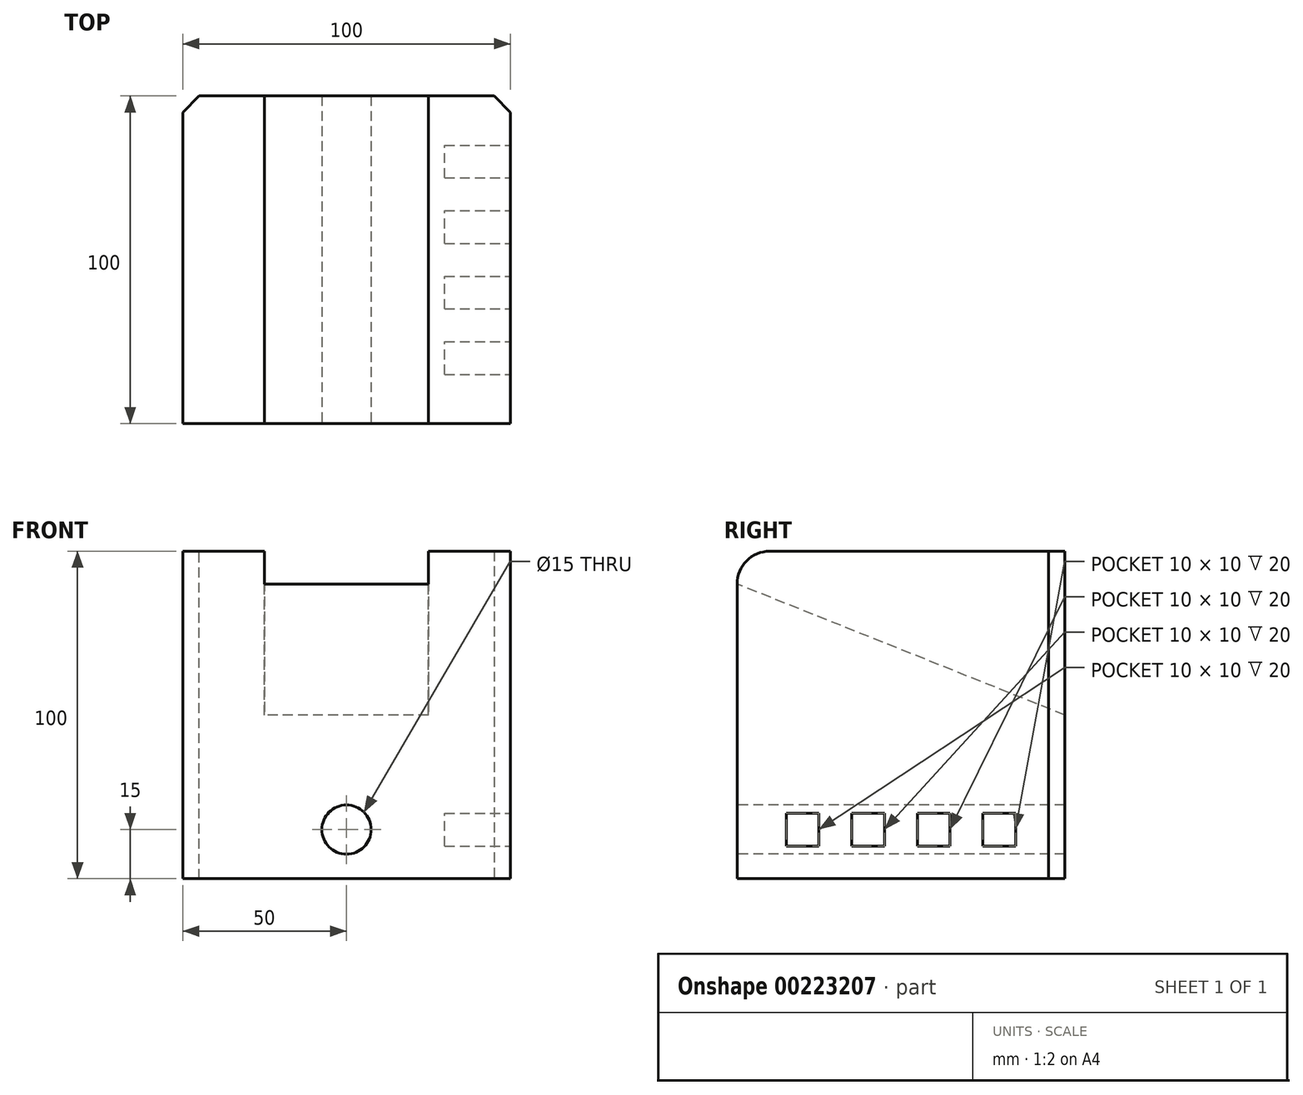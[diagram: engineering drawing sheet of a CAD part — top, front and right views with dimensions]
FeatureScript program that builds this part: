
annotation { "Feature Type Name" : "Feature", "Feature Type Description" : "" }
export const myFeature = defineFeature(function(context is Context, id is Id, definition is map)
    precondition{}
    {
        {
            var Q0;
            Q0=qCreatedBy(makeId("Front.planeOp"),FACE);
            var sketch = newSketch(context, id + "F0", { "sketchPlane" : qUnion([Q0])});
            skLineSegment(sketch, "E0.bottom", {"start": v(0, 0) * mm, "end": v(-100, 0) * mm});
            skLineSegment(sketch, "E0.top", {"start": v(0, 100) * mm, "end": v(-100, 100) * mm});
            skLineSegment(sketch, "E0.left", {"start": v(0, 0) * mm, "end": v(0, 100) * mm});
            skLineSegment(sketch, "E0.right", {"start": v(-100, 0) * mm, "end": v(-100, 100) * mm});
            skLineSegment(sketch, "E1", {"start": v(0, 0) * mm, "end": v(-50, 0) * mm, "construction": true});
            skLineSegment(sketch, "E2", {"start": v(-50, 0) * mm, "end": v(-50, 15) * mm, "construction": true});
            skCircle(sketch, "E3", {"center": v(-50, 15) * mm, "radius": 7.5 * mm});
            skSolve(sketch);
        }
        {
            var Q0;
            Q0 = qSketchRegion(id + "F0", true);
            extrude(context, id + "F1", {"entities" : qUnion([Q0]), "oppositeDirection" : true, "depth" : 100 * mm});
        }
        {
            var Q0;
            Q0=makeQuery(id+"F1.opExtrude","SWEPT_FACE",FACE,{"disambiguationData":[OSD([sQuery(id+"F0.wireOp",EDGE,"E0.left")])]});
            var Q1;
            Q1=makeQuery(id+"F1.opExtrude","SWEPT_FACE",FACE,{"disambiguationData":[OSD([sQuery(id+"F0.wireOp",EDGE,"E0.right")])]});
            cPlane(context, id + "F2", {"entities" : qUnion([Q0, Q1]), "cplaneType" : CPlaneType.MID_PLANE, "offset" : 25 * mm, "width" : 150 * mm, "height" : 150 * mm});
        }
        {
            var Q0;
            Q0=qCreatedBy(id+"F2.planeOp",FACE);
            var sketch = newSketch(context, id + "F3", { "sketchPlane" : qUnion([Q0])});
            skLineSegment(sketch, "E4", {"start": v(0, 90) * mm, "end": v(0, 100) * mm});
            skLineSegment(sketch, "E5", {"start": v(0, 100) * mm, "end": v(100, 100) * mm});
            skLineSegment(sketch, "E6", {"start": v(100, 100) * mm, "end": v(100, 50) * mm});
            skLineSegment(sketch, "E7", {"start": v(100, 50) * mm, "end": v(0, 90) * mm});
            skLineSegment(sketch, "E8", {"start": v(0, 90) * mm, "end": v(0, 0) * mm, "construction": true});
            skSolve(sketch);
        }
        {
            var Q0;
            Q0 = qSketchRegion(id + "F3", true);
            extrude(context, id + "F4", {"entities" : qUnion([Q0]), "operationType" : NewBodyOperationType.REMOVE, "endBound" : BoundingType.SYMMETRIC, "depth" : 50 * mm});
        }
        {
            var Q0;
            {var subQ0=sQuery(id+"F0.wireOp",EDGE,"E0.left");var subQ1=sQuery(id+"F0.wireOp",EDGE,"E0.top");Q0=makeQuery(id+"F4.boolean.opBoolean","SPLIT",EDGE,{"disambiguationData":[TD([makeQuery(id+"F1.opExtrude","SWEPT_FACE",FACE,{"disambiguationData":[OSD([subQ0])]})])],"derivedFrom":makeQuery(id+"F1.opExtrude","CAP_EDGE",EDGE,{"disambiguationData":[OSD([subQ1])],"isStart":true})});}
            var Q1;
            {var subQ0=sQuery(id+"F0.wireOp",EDGE,"E0.right");var subQ1=sQuery(id+"F0.wireOp",EDGE,"E0.top");Q1=makeQuery(id+"F4.boolean.opBoolean","SPLIT",EDGE,{"disambiguationData":[TD([makeQuery(id+"F1.opExtrude","SWEPT_FACE",FACE,{"disambiguationData":[OSD([subQ0])]})])],"derivedFrom":makeQuery(id+"F1.opExtrude","CAP_EDGE",EDGE,{"disambiguationData":[OSD([subQ1])],"isStart":true})});}
            fillet(context, id + "F5", {"entities" : qUnion([Q0, Q1]), "radius" : 10 * mm, "tangentPropagation" : true, "allowEdgeOverflow" : false});
        }
        {
            var Q0;
            Q0=makeQuery(id+"F1.opExtrude","CAP_EDGE",EDGE,{"disambiguationData":[OSD([sQuery(id+"F0.wireOp",EDGE,"E0.left")])],"isStart":false});
            var Q1;
            Q1=makeQuery(id+"F1.opExtrude","CAP_EDGE",EDGE,{"disambiguationData":[OSD([sQuery(id+"F0.wireOp",EDGE,"E0.right")])],"isStart":false});
            chamfer(context, id + "F6", {"entities" : qUnion([Q0, Q1]), "width" : 5 * mm, "tangentPropagation" : true});
        }
        {
            var Q0;
            Q0=qCreatedBy(makeId("Right.planeOp"),FACE);
            var sketch = newSketch(context, id + "F7", { "sketchPlane" : qUnion([Q0])});
            skLineSegment(sketch, "E9", {"start": v(0, 0) * mm, "end": v(15, 0) * mm, "construction": true});
            skLineSegment(sketch, "E10", {"start": v(15, 0) * mm, "end": v(15, 10) * mm, "construction": true});
            skLineSegment(sketch, "E11.bottom", {"start": v(15, 10) * mm, "end": v(25, 10) * mm});
            skLineSegment(sketch, "E11.top", {"start": v(15, 20) * mm, "end": v(25, 20) * mm});
            skLineSegment(sketch, "E11.left", {"start": v(15, 10) * mm, "end": v(15, 20) * mm});
            skLineSegment(sketch, "E11.right", {"start": v(25, 10) * mm, "end": v(25, 20) * mm});
            skLineSegment(sketch, "E12.1.0.0", {"start": v(35, 20) * mm, "end": v(45, 20) * mm});
            skLineSegment(sketch, "E12.1.0.1", {"start": v(45, 10) * mm, "end": v(45, 20) * mm});
            skLineSegment(sketch, "E12.1.0.2", {"start": v(35, 10) * mm, "end": v(45, 10) * mm});
            skLineSegment(sketch, "E12.1.0.3", {"start": v(35, 10) * mm, "end": v(35, 20) * mm});
            skLineSegment(sketch, "E12.2.0.0", {"start": v(55, 20) * mm, "end": v(65, 20) * mm});
            skLineSegment(sketch, "E12.2.0.1", {"start": v(65, 10) * mm, "end": v(65, 20) * mm});
            skLineSegment(sketch, "E12.2.0.2", {"start": v(55, 10) * mm, "end": v(65, 10) * mm});
            skLineSegment(sketch, "E12.2.0.3", {"start": v(55, 10) * mm, "end": v(55, 20) * mm});
            skLineSegment(sketch, "E12.3.0.0", {"start": v(75, 20) * mm, "end": v(85, 20) * mm});
            skLineSegment(sketch, "E12.3.0.1", {"start": v(85, 10) * mm, "end": v(85, 20) * mm});
            skLineSegment(sketch, "E12.3.0.2", {"start": v(75, 10) * mm, "end": v(85, 10) * mm});
            skLineSegment(sketch, "E12.3.0.3", {"start": v(75, 10) * mm, "end": v(75, 20) * mm});
            skLineSegment(sketch, "E12.direction1", {"start": v(15, 20) * mm, "end": v(35, 20) * mm, "construction": true});
            skSolve(sketch);
        }
        {
            var Q0;
            Q0 = qSketchRegion(id + "F7", true);
            extrude(context, id + "F8", {"entities" : qUnion([Q0]), "operationType" : NewBodyOperationType.REMOVE, "oppositeDirection" : true, "depth" : 20 * mm});
        }
    });
